# Revit family: Bernhardt-Design_Seating_Neighborhood_MobileSeating
name_source: partatom
category: Furniture
revit_build: Autodesk Revit 2016 (Build: 20150714_1515(x64)
units: mm (PartAtom-declared; Revit-internal decimal feet)

## family parameters
Always vertical = Yes
Cut with Voids When Loaded = No
OmniClass Number = 23.40.20.00
OmniClass Title = General Furniture and Specialties
Room Calculation Point = No
Shared = No
Work Plane-Based = No

## types (6) — shared parameters
Manufacturer = Bernhardt Design
Model = Neighborhood
URL = http://www.bernhardtdesign.com

## per-type parameters (varying)
| type | 6021 | 6024 | 6030 | Handle Finish | Type Selection |
| 6024M | No | Yes | No | <By Category> | 6024 |
| 6030MB | No | No | Yes | Brushed Aluminum | 6030 |
| 6021M | Yes | No | No | Aluminum - Brushed | 6021 |
| 6021MJ | Yes | No | No | <By Category> | 60211 |
| 6024MJ | No | Yes | No | <By Category> | 60241 |
| 6030MBJ | No | No | Yes | Brushed Aluminum | 60301 |

## geometry (parser evidence)
native form markers: Sweep x10
no freeform markers — native parametric forms only
